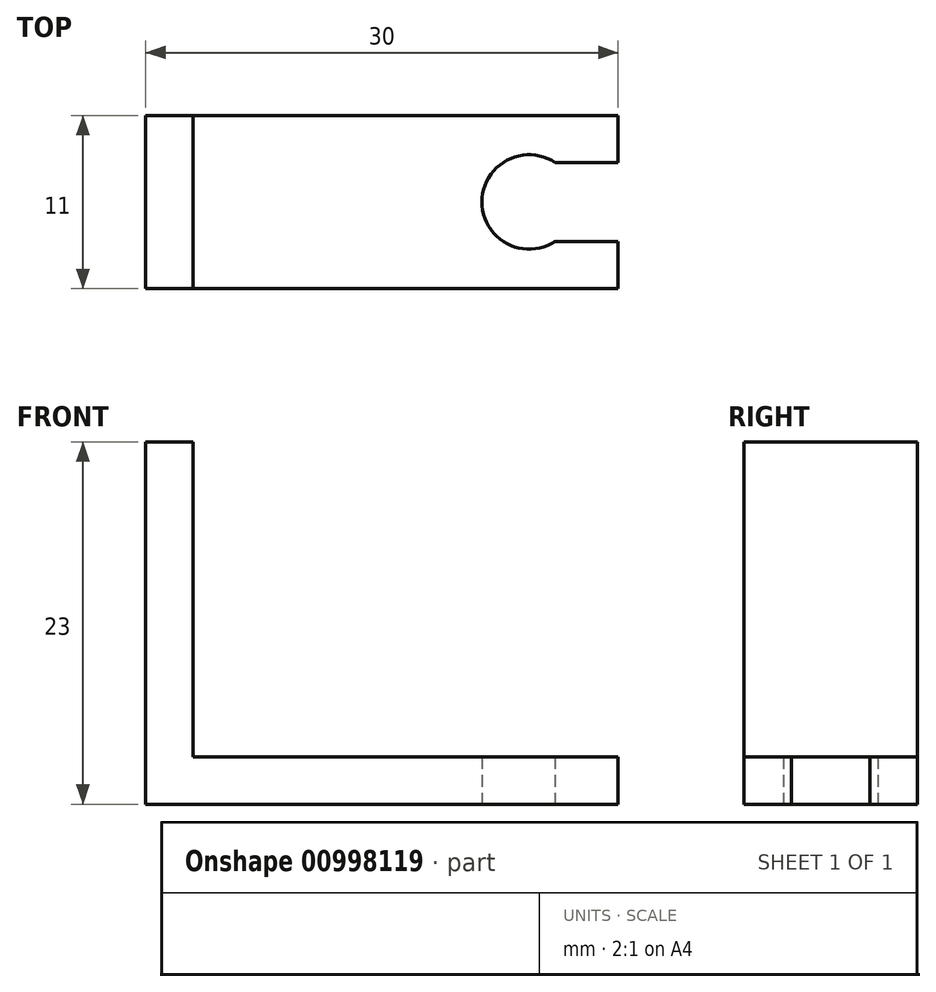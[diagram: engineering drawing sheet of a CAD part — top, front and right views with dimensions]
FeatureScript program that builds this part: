
annotation { "Feature Type Name" : "Feature", "Feature Type Description" : "" }
export const myFeature = defineFeature(function(context is Context, id is Id, definition is map)
    precondition{}
    {
        {
            var Q0;
            Q0=qCreatedBy(makeId("Top.planeOp"),FACE);
            var sketch = newSketch(context, id + "F0", { "sketchPlane" : qUnion([Q0])});
            skLineSegment(sketch, "E0", {"start": v(0, 0) * mm, "end": v(29.97, 0) * mm, "construction": true});
            skLineSegment(sketch, "E1", {"start": v(0, 0) * mm, "end": v(0, -5.5) * mm});
            skLineSegment(sketch, "E2", {"start": v(0, -5.5) * mm, "end": v(30, -5.5) * mm});
            skLineSegment(sketch, "E3", {"start": v(30, -5.5) * mm, "end": v(30, -2.5) * mm});
            skLineSegment(sketch, "E4", {"start": v(30, -2.5) * mm, "end": v(26, -2.5) * mm});
            skArc(sketch, "E5", {"start": v(21.34, 0) * mm, "mid": v(22.92, -2.64) * mm, "end": v(26, -2.5) * mm});
            skArc(sketch, "E6.MirrorCS", {"start": v(21.34, 0) * mm, "mid": v(22.92, 2.64) * mm, "end": v(26, 2.5) * mm});
            skLineSegment(sketch, "E7.MirrorCS", {"start": v(30, 2.5) * mm, "end": v(26, 2.5) * mm});
            skLineSegment(sketch, "E8.MirrorCS", {"start": v(30, 5.5) * mm, "end": v(30, 2.5) * mm});
            skLineSegment(sketch, "E9.MirrorCS", {"start": v(0, 5.5) * mm, "end": v(30, 5.5) * mm});
            skLineSegment(sketch, "E10.MirrorCS", {"start": v(0, 0) * mm, "end": v(0, 5.5) * mm});
            skSolve(sketch);
        }
        {
            var Q0;
            Q0 = qSketchRegion(id + "F0", true);
            extrude(context, id + "F1", {"entities" : qUnion([Q0]), "depth" : 3 * mm, "offsetDistance" : 25 * mm});
        }
        {
            var Q0;
            Q0=makeQuery(id+"F1.opExtrude","CAP_FACE",FACE,{"disambiguationData":[OSD([sQuery(id+"F0.wireOp",EDGE,"E1"),sQuery(id+"F0.wireOp",EDGE,"E2"),sQuery(id+"F0.wireOp",EDGE,"E3"),sQuery(id+"F0.wireOp",EDGE,"E4"),sQuery(id+"F0.wireOp",EDGE,"E5"),sQuery(id+"F0.wireOp",EDGE,"E6.MirrorCS"),sQuery(id+"F0.wireOp",EDGE,"E7.MirrorCS"),sQuery(id+"F0.wireOp",EDGE,"E8.MirrorCS"),sQuery(id+"F0.wireOp",EDGE,"E9.MirrorCS"),sQuery(id+"F0.wireOp",EDGE,"E10.MirrorCS")])],"isStart":false});
            var sketch = newSketch(context, id + "F2", { "sketchPlane" : qUnion([Q0])});
            skLineSegment(sketch, "E11.bottom", {"start": v(0, 5.5) * mm, "end": v(3, 5.5) * mm});
            skLineSegment(sketch, "E11.top", {"start": v(0, -5.5) * mm, "end": v(3, -5.5) * mm});
            skLineSegment(sketch, "E11.left", {"start": v(0, 5.5) * mm, "end": v(0, -5.5) * mm});
            skLineSegment(sketch, "E11.right", {"start": v(3, 5.5) * mm, "end": v(3, -5.5) * mm});
            skSolve(sketch);
        }
        {
            var Q0;
            Q0 = qSketchRegion(id + "F2", true);
            extrude(context, id + "F3", {"entities" : qUnion([Q0]), "operationType" : NewBodyOperationType.ADD, "depth" : 20 * mm, "offsetDistance" : 25 * mm});
        }
    });
